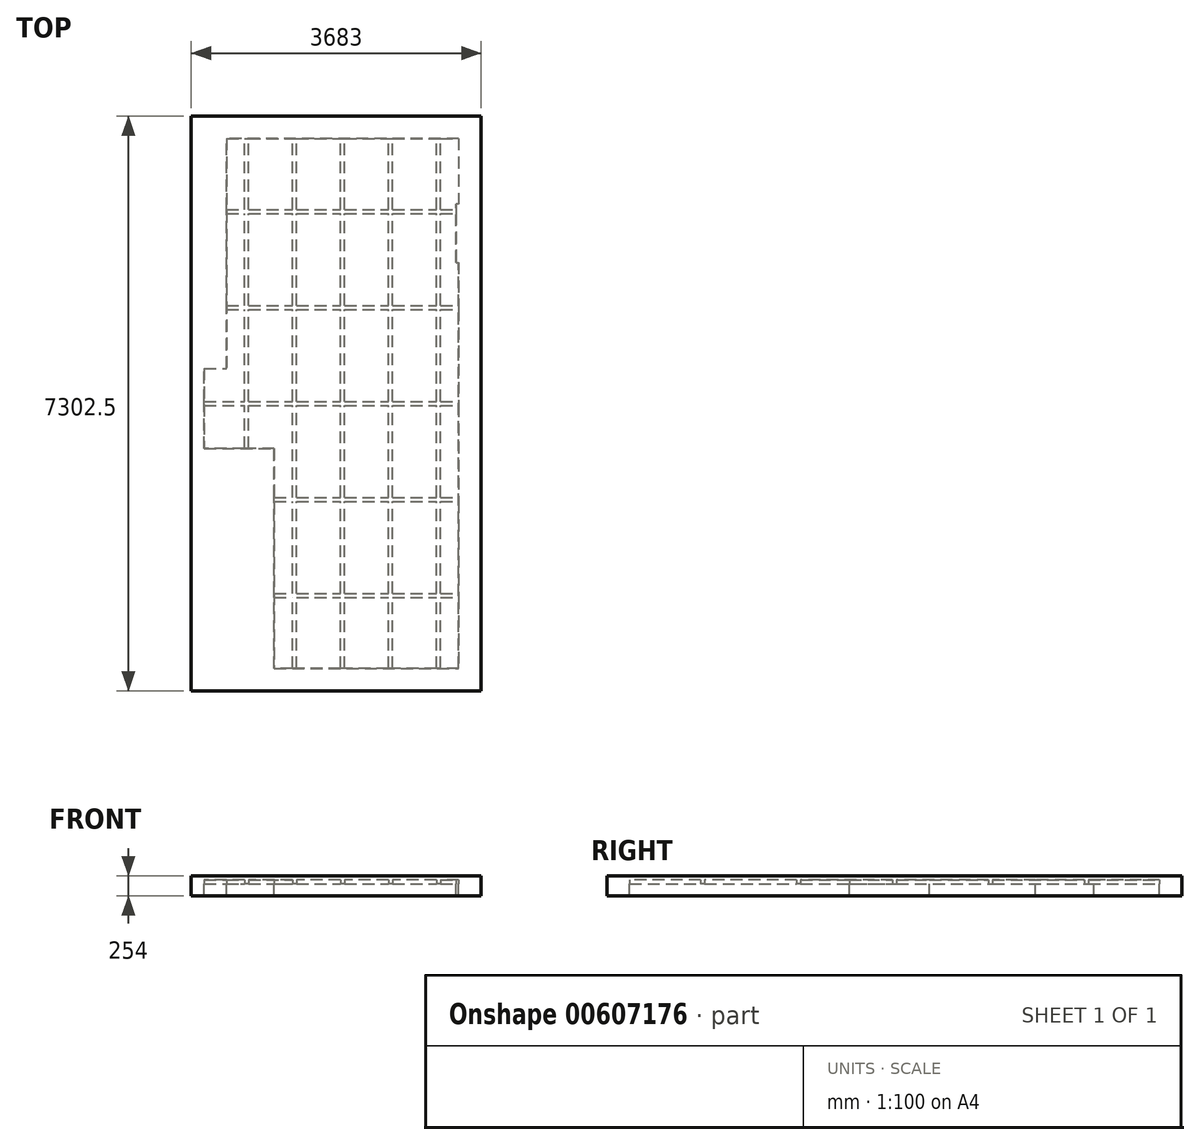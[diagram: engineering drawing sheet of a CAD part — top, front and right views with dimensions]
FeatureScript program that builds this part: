
annotation { "Feature Type Name" : "Feature", "Feature Type Description" : "" }
export const myFeature = defineFeature(function(context is Context, id is Id, definition is map)
    precondition{}
    {
        {
            var Q0;
            Q0=qCreatedBy(makeId("Top.planeOp"),FACE);
            var sketch = newSketch(context, id + "F0", { "sketchPlane" : qUnion([Q0])});
            skLineSegment(sketch, "E0", {"start": v(0, 0) * mm, "end": v(0, 5156.2) * mm});
            skLineSegment(sketch, "E1", {"start": v(0, 5156.2) * mm, "end": v(-34.92, 5156.2) * mm});
            skLineSegment(sketch, "E2", {"start": v(-34.92, 5156.2) * mm, "end": v(-34.92, 5899.15) * mm});
            skLineSegment(sketch, "E3", {"start": v(-34.92, 5899.15) * mm, "end": v(0, 5899.15) * mm});
            skLineSegment(sketch, "E4", {"start": v(0, 5899.15) * mm, "end": v(0, 6731) * mm});
            skLineSegment(sketch, "E5", {"start": v(0, 6731) * mm, "end": v(-2946.4, 6731) * mm});
            skLineSegment(sketch, "E6", {"start": v(-2946.4, 6731) * mm, "end": v(-2946.4, 3810) * mm});
            skLineSegment(sketch, "E7", {"start": v(-2946.4, 3810) * mm, "end": v(-3232.15, 3810) * mm});
            skLineSegment(sketch, "E8", {"start": v(-3232.15, 3810) * mm, "end": v(-3232.15, 2794) * mm});
            skLineSegment(sketch, "E9", {"start": v(-3232.15, 2794) * mm, "end": v(-2343.15, 2794) * mm});
            skLineSegment(sketch, "E10", {"start": v(-2343.15, 2794) * mm, "end": v(-2343.15, 0) * mm});
            skLineSegment(sketch, "E11", {"start": v(-2343.15, 0) * mm, "end": v(0, 0) * mm});
            skLineSegment(sketch, "E12", {"start": v(285.75, 7016.75) * mm, "end": v(285.75, -285.75) * mm});
            skLineSegment(sketch, "E13", {"start": v(285.75, -285.75) * mm, "end": v(-3397.25, -285.75) * mm});
            skLineSegment(sketch, "E14", {"start": v(285.75, 7016.75) * mm, "end": v(-3397.25, 7016.75) * mm});
            skLineSegment(sketch, "E15", {"start": v(-3397.25, 7016.75) * mm, "end": v(-3397.25, -285.75) * mm});
            skSolve(sketch);
        }
        {
            var Q0;
            Q0=makeQuery(id+"F0.imprint","IMPRINT",FACE,{"disambiguationData":[TD([[makeQuery(id+"F0.imprint","IMPRINT",EDGE,{"derivedFrom":sQuery(id+"F0.wireOp",EDGE,"E0")}),-1.0]])]});
            extrude(context, id + "F1", {"entities" : qUnion([Q0]), "oppositeDirection" : true, "depth" : 254 * mm, "offsetDistance" : 25.4 * mm});
        }
        {
            var Q0;
            Q0=qSketchRegion(id+"F0",true);
            var Q1;
            Q1=makeQuery(id+"F0.imprint","IMPRINT",FACE,{"disambiguationData":[TD([[makeQuery(id+"F0.imprint","IMPRINT",EDGE,{"derivedFrom":sQuery(id+"F0.wireOp",EDGE,"E0")}),1.0]])]});
            extrude(context, id + "F2", {"entities" : qUnion([Q0, Q1]), "operationType" : NewBodyOperationType.ADD, "oppositeDirection" : true, "depth" : 101.6 * mm, "offsetDistance" : 25.4 * mm});
        }
        {
            var Q0;
            Q0=makeQuery(id+"F2.opExtrude","CAP_FACE",FACE,{"disambiguationData":[OSD([sQuery(id+"F0.wireOp",EDGE,"E12"),sQuery(id+"F0.wireOp",EDGE,"E13"),sQuery(id+"F0.wireOp",EDGE,"E14"),sQuery(id+"F0.wireOp",EDGE,"E15")])],"isStart":false});
            var sketch = newSketch(context, id + "F3", { "sketchPlane" : qUnion([Q0])});
            skLineSegment(sketch, "E16.bottom", {"start": v(-2060.58, 0) * mm, "end": v(-2111.38, 0) * mm});
            skLineSegment(sketch, "E16.top", {"start": v(-2060.57, -6731) * mm, "end": v(-2111.37, -6731) * mm});
            skLineSegment(sketch, "E16.left", {"start": v(-2060.58, 0) * mm, "end": v(-2060.58, -901.7) * mm});
            skLineSegment(sketch, "E17.bottom", {"start": v(-1450.98, 0) * mm, "end": v(-1501.78, 0) * mm});
            skLineSegment(sketch, "E17.top", {"start": v(-1450.97, -6731) * mm, "end": v(-1501.77, -6731) * mm});
            skLineSegment(sketch, "E17.left", {"start": v(-1450.98, 0) * mm, "end": v(-1450.98, -901.7) * mm});
            skLineSegment(sketch, "E17.right", {"start": v(-1501.78, 0) * mm, "end": v(-1501.78, -901.7) * mm});
            skPoint(sketch, "E18.oppositeSnap0", {"position": v(-892.18, 0) * mm});
            skLineSegment(sketch, "E18.bottom", {"start": v(-841.38, 0) * mm, "end": v(-892.18, 0) * mm});
            skLineSegment(sketch, "E18.top", {"start": v(-841.37, -6731) * mm, "end": v(-892.17, -6731) * mm});
            skLineSegment(sketch, "E18.left", {"start": v(-841.38, 0) * mm, "end": v(-841.38, -901.7) * mm});
            skLineSegment(sketch, "E18.right", {"start": v(-892.18, 0) * mm, "end": v(-892.18, -901.7) * mm});
            skLineSegment(sketch, "E19.bottom", {"start": v(-282.58, 0) * mm, "end": v(-231.78, 0) * mm});
            skLineSegment(sketch, "E19.top", {"start": v(-282.57, -6731) * mm, "end": v(-231.77, -6731) * mm});
            skLineSegment(sketch, "E19.left", {"start": v(-282.58, 0) * mm, "end": v(-282.57, -901.7) * mm});
            skLineSegment(sketch, "E19.right", {"start": v(-231.78, 0) * mm, "end": v(-231.77, -901.7) * mm});
            skLineSegment(sketch, "E20.bottom", {"start": v(-2720.98, -2794) * mm, "end": v(-2670.18, -2794) * mm});
            skLineSegment(sketch, "E20.top", {"start": v(-2720.98, -6731) * mm, "end": v(-2670.18, -6731) * mm});
            skLineSegment(sketch, "E20.left", {"start": v(-2720.98, -2794) * mm, "end": v(-2720.98, -3340.1) * mm});
            skLineSegment(sketch, "E20.right", {"start": v(-2670.18, -5829.3) * mm, "end": v(-2670.18, -6731) * mm});
            skLineSegment(sketch, "E21.bottom", {"start": v(-231.77, -5829.3) * mm, "end": v(-34.92, -5829.3) * mm});
            skLineSegment(sketch, "E21.top", {"start": v(-2946.4, -5778.5) * mm, "end": v(-2720.98, -5778.5) * mm});
            skLineSegment(sketch, "E21.left", {"start": v(-2946.4, -5829.3) * mm, "end": v(-2946.4, -5778.5) * mm});
            skLineSegment(sketch, "E21.right", {"start": v(-34.92, -5829.3) * mm, "end": v(-34.92, -5778.5) * mm});
            skLineSegment(sketch, "E22.bottom", {"start": v(-231.77, -4559.3) * mm, "end": v(0, -4559.3) * mm});
            skLineSegment(sketch, "E22.top", {"start": v(-2946.4, -4610.1) * mm, "end": v(-2720.98, -4610.1) * mm});
            skLineSegment(sketch, "E22.left", {"start": v(-2946.4, -4559.3) * mm, "end": v(-2946.4, -4610.1) * mm});
            skLineSegment(sketch, "E22.right", {"start": v(0, -4559.3) * mm, "end": v(0, -4610.1) * mm});
            skLineSegment(sketch, "E23.bottom", {"start": v(-3232.15, -3340.1) * mm, "end": v(-2720.98, -3340.1) * mm});
            skLineSegment(sketch, "E23.top", {"start": v(-3232.15, -3390.9) * mm, "end": v(-2720.98, -3390.9) * mm});
            skLineSegment(sketch, "E23.left", {"start": v(-3232.15, -3340.1) * mm, "end": v(-3232.15, -3390.9) * mm});
            skLineSegment(sketch, "E23.right", {"start": v(0, -3340.1) * mm, "end": v(0, -3390.9) * mm});
            skLineSegment(sketch, "E24.bottom", {"start": v(-231.77, -2120.9) * mm, "end": v(0, -2120.9) * mm});
            skLineSegment(sketch, "E24.top", {"start": v(-2343.15, -2171.7) * mm, "end": v(-2111.38, -2171.7) * mm});
            skLineSegment(sketch, "E24.left", {"start": v(-2343.15, -2120.9) * mm, "end": v(-2343.15, -2171.7) * mm});
            skLineSegment(sketch, "E24.right", {"start": v(0, -2120.9) * mm, "end": v(0, -2171.7) * mm});
            skLineSegment(sketch, "E25.bottom", {"start": v(-231.77, -901.7) * mm, "end": v(0, -901.7) * mm});
            skLineSegment(sketch, "E25.top", {"start": v(-2343.15, -952.5) * mm, "end": v(-2111.38, -952.5) * mm});
            skLineSegment(sketch, "E25.left", {"start": v(-2343.15, -901.7) * mm, "end": v(-2343.15, -952.5) * mm});
            skLineSegment(sketch, "E25.right", {"start": v(0, -901.7) * mm, "end": v(0, -952.5) * mm});
            skLineSegment(sketch, "E26.trimOffspring", {"start": v(-2111.38, 0) * mm, "end": v(-2111.38, -901.7) * mm});
            skLineSegment(sketch, "E27.trimOffspring", {"start": v(-2111.38, -952.5) * mm, "end": v(-2111.38, -2120.9) * mm});
            skLineSegment(sketch, "E28.trimOffspring", {"start": v(-2343.15, -901.7) * mm, "end": v(-2111.38, -901.7) * mm});
            skLineSegment(sketch, "E29.trimOffspring", {"start": v(-2060.58, -952.5) * mm, "end": v(-2060.57, -2120.9) * mm});
            skLineSegment(sketch, "E30.trimOffspring", {"start": v(-2060.58, -952.5) * mm, "end": v(-1501.78, -952.5) * mm});
            skLineSegment(sketch, "E31.trimOffspring", {"start": v(-1501.78, -952.5) * mm, "end": v(-1501.78, -2120.9) * mm});
            skLineSegment(sketch, "E32.trimOffspring", {"start": v(-2060.58, -901.7) * mm, "end": v(-1501.78, -901.7) * mm});
            skLineSegment(sketch, "E33.trimOffspring", {"start": v(-1450.98, -952.5) * mm, "end": v(-1450.98, -2120.9) * mm});
            skLineSegment(sketch, "E34.trimOffspring", {"start": v(-1450.98, -952.5) * mm, "end": v(-892.18, -952.5) * mm});
            skLineSegment(sketch, "E35.trimOffspring", {"start": v(-1450.98, -901.7) * mm, "end": v(-892.18, -901.7) * mm});
            skLineSegment(sketch, "E36.trimOffspring", {"start": v(-892.18, -952.5) * mm, "end": v(-892.18, -2120.9) * mm});
            skLineSegment(sketch, "E37.trimOffspring", {"start": v(-841.38, -952.5) * mm, "end": v(-282.58, -952.5) * mm});
            skLineSegment(sketch, "E38.trimOffspring", {"start": v(-841.38, -952.5) * mm, "end": v(-841.38, -2120.9) * mm});
            skLineSegment(sketch, "E39.trimOffspring", {"start": v(-841.38, -901.7) * mm, "end": v(-282.58, -901.7) * mm});
            skLineSegment(sketch, "E40.trimOffspring", {"start": v(-282.57, -952.5) * mm, "end": v(-282.57, -2120.9) * mm});
            skLineSegment(sketch, "E41.trimOffspring", {"start": v(-231.77, -952.5) * mm, "end": v(0, -952.5) * mm});
            skLineSegment(sketch, "E42.trimOffspring", {"start": v(-231.77, -952.5) * mm, "end": v(-231.77, -2120.9) * mm});
            skLineSegment(sketch, "E43.trimOffspring", {"start": v(-2111.38, -2171.7) * mm, "end": v(-2111.38, -3340.1) * mm});
            skLineSegment(sketch, "E44.trimOffspring", {"start": v(-2343.15, -2120.9) * mm, "end": v(-2111.38, -2120.9) * mm});
            skLineSegment(sketch, "E45.trimOffspring", {"start": v(-2060.57, -2171.7) * mm, "end": v(-2060.57, -3340.1) * mm});
            skLineSegment(sketch, "E46.trimOffspring", {"start": v(-2060.57, -2171.7) * mm, "end": v(-1501.78, -2171.7) * mm});
            skLineSegment(sketch, "E47.trimOffspring", {"start": v(-1501.78, -2171.7) * mm, "end": v(-1501.77, -3340.1) * mm});
            skLineSegment(sketch, "E48.trimOffspring", {"start": v(-2060.57, -2120.9) * mm, "end": v(-1501.78, -2120.9) * mm});
            skLineSegment(sketch, "E49.trimOffspring", {"start": v(-1450.98, -2171.7) * mm, "end": v(-1450.97, -3340.1) * mm});
            skLineSegment(sketch, "E50.trimOffspring", {"start": v(-1450.98, -2171.7) * mm, "end": v(-892.18, -2171.7) * mm});
            skLineSegment(sketch, "E51.trimOffspring", {"start": v(-892.18, -2171.7) * mm, "end": v(-892.18, -3340.1) * mm});
            skLineSegment(sketch, "E52.trimOffspring", {"start": v(-1450.98, -2120.9) * mm, "end": v(-892.18, -2120.9) * mm});
            skLineSegment(sketch, "E53.trimOffspring", {"start": v(-841.38, -2171.7) * mm, "end": v(-841.37, -3340.1) * mm});
            skLineSegment(sketch, "E54.trimOffspring", {"start": v(-841.38, -2171.7) * mm, "end": v(-282.57, -2171.7) * mm});
            skLineSegment(sketch, "E55.trimOffspring", {"start": v(-282.57, -2171.7) * mm, "end": v(-282.57, -3340.1) * mm});
            skLineSegment(sketch, "E56.trimOffspring", {"start": v(-841.38, -2120.9) * mm, "end": v(-282.57, -2120.9) * mm});
            skLineSegment(sketch, "E57.trimOffspring", {"start": v(-231.77, -2171.7) * mm, "end": v(-231.77, -3340.1) * mm});
            skLineSegment(sketch, "E58.trimOffspring", {"start": v(-231.77, -2171.7) * mm, "end": v(0, -2171.7) * mm});
            skLineSegment(sketch, "E59.trimOffspring", {"start": v(-2720.98, -3390.9) * mm, "end": v(-2720.98, -4559.3) * mm});
            skLineSegment(sketch, "E60.trimOffspring", {"start": v(-2670.18, -3340.1) * mm, "end": v(-2111.38, -3340.1) * mm});
            skLineSegment(sketch, "E61.trimOffspring", {"start": v(-2670.18, -2794) * mm, "end": v(-2670.18, -3340.1) * mm});
            skLineSegment(sketch, "E62.trimOffspring", {"start": v(-2670.18, -3390.9) * mm, "end": v(-2111.38, -3390.9) * mm});
            skLineSegment(sketch, "E63.trimOffspring", {"start": v(-2111.38, -3390.9) * mm, "end": v(-2111.37, -4559.3) * mm});
            skLineSegment(sketch, "E64.trimOffspring", {"start": v(-2060.57, -3340.1) * mm, "end": v(-1501.77, -3340.1) * mm});
            skLineSegment(sketch, "E65.trimOffspring", {"start": v(-2060.57, -3390.9) * mm, "end": v(-2060.57, -4559.3) * mm});
            skLineSegment(sketch, "E66.trimOffspring", {"start": v(-2060.57, -3390.9) * mm, "end": v(-1501.77, -3390.9) * mm});
            skLineSegment(sketch, "E67.trimOffspring", {"start": v(-1501.77, -3390.9) * mm, "end": v(-1501.77, -4559.3) * mm});
            skLineSegment(sketch, "E68.trimOffspring", {"start": v(-1450.97, -3340.1) * mm, "end": v(-892.18, -3340.1) * mm});
            skLineSegment(sketch, "E69.trimOffspring", {"start": v(-1450.97, -3390.9) * mm, "end": v(-1450.97, -4559.3) * mm});
            skLineSegment(sketch, "E70.trimOffspring", {"start": v(-1450.97, -3390.9) * mm, "end": v(-892.18, -3390.9) * mm});
            skLineSegment(sketch, "E71.trimOffspring", {"start": v(-892.18, -3390.9) * mm, "end": v(-892.17, -4559.3) * mm});
            skLineSegment(sketch, "E72.trimOffspring", {"start": v(-841.37, -3340.1) * mm, "end": v(-282.57, -3340.1) * mm});
            skLineSegment(sketch, "E73.trimOffspring", {"start": v(-841.37, -3390.9) * mm, "end": v(-841.37, -4559.3) * mm});
            skLineSegment(sketch, "E74.trimOffspring", {"start": v(-841.37, -3390.9) * mm, "end": v(-282.57, -3390.9) * mm});
            skLineSegment(sketch, "E75.trimOffspring", {"start": v(-282.57, -3390.9) * mm, "end": v(-282.57, -4559.3) * mm});
            skLineSegment(sketch, "E76.trimOffspring", {"start": v(-231.77, -3340.1) * mm, "end": v(0, -3340.1) * mm});
            skLineSegment(sketch, "E77.trimOffspring", {"start": v(-231.77, -3390.9) * mm, "end": v(-231.77, -4559.3) * mm});
            skLineSegment(sketch, "E78.trimOffspring", {"start": v(-231.77, -3390.9) * mm, "end": v(0, -3390.9) * mm});
            skLineSegment(sketch, "E79.trimOffspring", {"start": v(-2720.98, -4610.1) * mm, "end": v(-2720.98, -5778.5) * mm});
            skLineSegment(sketch, "E80.trimOffspring", {"start": v(-2946.4, -4559.3) * mm, "end": v(-2720.98, -4559.3) * mm});
            skLineSegment(sketch, "E81.trimOffspring", {"start": v(-2670.18, -3390.9) * mm, "end": v(-2670.18, -4559.3) * mm});
            skLineSegment(sketch, "E82.trimOffspring", {"start": v(-2670.18, -4610.1) * mm, "end": v(-2111.37, -4610.1) * mm});
            skLineSegment(sketch, "E83.trimOffspring", {"start": v(-2111.37, -4610.1) * mm, "end": v(-2111.37, -5778.5) * mm});
            skLineSegment(sketch, "E84.trimOffspring", {"start": v(-2670.18, -4559.3) * mm, "end": v(-2111.37, -4559.3) * mm});
            skLineSegment(sketch, "E85.trimOffspring", {"start": v(-2060.57, -4610.1) * mm, "end": v(-2060.57, -5778.5) * mm});
            skLineSegment(sketch, "E86.trimOffspring", {"start": v(-2060.57, -4610.1) * mm, "end": v(-1501.77, -4610.1) * mm});
            skLineSegment(sketch, "E87.trimOffspring", {"start": v(-1501.77, -4610.1) * mm, "end": v(-1501.77, -5778.5) * mm});
            skLineSegment(sketch, "E88.trimOffspring", {"start": v(-2060.57, -4559.3) * mm, "end": v(-1501.77, -4559.3) * mm});
            skLineSegment(sketch, "E89.trimOffspring", {"start": v(-1450.97, -4610.1) * mm, "end": v(-1450.97, -5778.5) * mm});
            skLineSegment(sketch, "E90.trimOffspring", {"start": v(-1450.97, -4610.1) * mm, "end": v(-892.17, -4610.1) * mm});
            skLineSegment(sketch, "E91.trimOffspring", {"start": v(-892.17, -4610.1) * mm, "end": v(-892.17, -5778.5) * mm});
            skLineSegment(sketch, "E92.trimOffspring", {"start": v(-1450.97, -4559.3) * mm, "end": v(-892.17, -4559.3) * mm});
            skLineSegment(sketch, "E93.trimOffspring", {"start": v(-841.37, -4610.1) * mm, "end": v(-841.37, -5778.5) * mm});
            skLineSegment(sketch, "E94.trimOffspring", {"start": v(-841.37, -4610.1) * mm, "end": v(-282.57, -4610.1) * mm});
            skLineSegment(sketch, "E95.trimOffspring", {"start": v(-282.57, -4610.1) * mm, "end": v(-282.57, -5778.5) * mm});
            skLineSegment(sketch, "E96.trimOffspring", {"start": v(-841.37, -4559.3) * mm, "end": v(-282.57, -4559.3) * mm});
            skLineSegment(sketch, "E97.trimOffspring", {"start": v(-231.77, -4610.1) * mm, "end": v(-231.77, -5778.5) * mm});
            skLineSegment(sketch, "E98.trimOffspring", {"start": v(-231.77, -4610.1) * mm, "end": v(0, -4610.1) * mm});
            skLineSegment(sketch, "E99.trimOffspring", {"start": v(-2720.98, -5829.3) * mm, "end": v(-2720.98, -6731) * mm});
            skLineSegment(sketch, "E100.trimOffspring", {"start": v(-2670.18, -5778.5) * mm, "end": v(-2111.37, -5778.5) * mm});
            skLineSegment(sketch, "E101.trimOffspring", {"start": v(-2670.18, -4610.1) * mm, "end": v(-2670.18, -5778.5) * mm});
            skLineSegment(sketch, "E102.trimOffspring", {"start": v(-2946.4, -5829.3) * mm, "end": v(-2720.98, -5829.3) * mm});
            skLineSegment(sketch, "E103.trimOffspring", {"start": v(-2111.37, -5829.3) * mm, "end": v(-2111.37, -6731) * mm});
            skLineSegment(sketch, "E104.trimOffspring", {"start": v(-2060.57, -5778.5) * mm, "end": v(-1501.77, -5778.5) * mm});
            skLineSegment(sketch, "E105.trimOffspring", {"start": v(-2060.57, -5829.3) * mm, "end": v(-2060.57, -6731) * mm});
            skLineSegment(sketch, "E106.trimOffspring", {"start": v(-2670.18, -5829.3) * mm, "end": v(-2111.37, -5829.3) * mm});
            skLineSegment(sketch, "E107.trimOffspring", {"start": v(-1501.77, -5829.3) * mm, "end": v(-1501.77, -6731) * mm});
            skLineSegment(sketch, "E108.trimOffspring", {"start": v(-1450.97, -5778.5) * mm, "end": v(-892.17, -5778.5) * mm});
            skLineSegment(sketch, "E109.trimOffspring", {"start": v(-1450.97, -5829.3) * mm, "end": v(-1450.97, -6731) * mm});
            skLineSegment(sketch, "E110.trimOffspring", {"start": v(-2060.57, -5829.3) * mm, "end": v(-1501.77, -5829.3) * mm});
            skLineSegment(sketch, "E111.trimOffspring", {"start": v(-892.17, -5829.3) * mm, "end": v(-892.17, -6731) * mm});
            skLineSegment(sketch, "E112.trimOffspring", {"start": v(-841.37, -5778.5) * mm, "end": v(-282.57, -5778.5) * mm});
            skLineSegment(sketch, "E113.trimOffspring", {"start": v(-841.37, -5829.3) * mm, "end": v(-841.37, -6731) * mm});
            skLineSegment(sketch, "E114.trimOffspring", {"start": v(-1450.97, -5829.3) * mm, "end": v(-892.17, -5829.3) * mm});
            skLineSegment(sketch, "E115.trimOffspring", {"start": v(-282.57, -5829.3) * mm, "end": v(-282.57, -6731) * mm});
            skLineSegment(sketch, "E116.trimOffspring", {"start": v(-231.77, -5778.5) * mm, "end": v(-34.92, -5778.5) * mm});
            skLineSegment(sketch, "E117.trimOffspring", {"start": v(-231.77, -5829.3) * mm, "end": v(-231.77, -6731) * mm});
            skLineSegment(sketch, "E118.trimOffspring", {"start": v(-841.37, -5829.3) * mm, "end": v(-282.57, -5829.3) * mm});
            skSolve(sketch);
        }
        {
            var Q0;
            {var subQ0=sQuery(id+"F3.wireOp",EDGE,"E16.right");Q0=makeQuery(id+"F3.imprint","IMPRINT",FACE,{"disambiguationData":[TD([[makeQuery(id+"F3.imprint","IMPRINT",EDGE,{"derivedFrom":subQ0}),-1.0]])]});}
            var Q1;
            {var subQ0=sQuery(id+"F3.wireOp",EDGE,"E16.left");Q1=makeQuery(id+"F3.imprint","IMPRINT",FACE,{"disambiguationData":[TD([[makeQuery(id+"F3.imprint","IMPRINT",EDGE,{"derivedFrom":subQ0}),1.0]])]});}
            var Q2;
            {var subQ0=sQuery(id+"F3.wireOp",EDGE,"E17.left");Q2=makeQuery(id+"F3.imprint","IMPRINT",FACE,{"disambiguationData":[TD([[makeQuery(id+"F3.imprint","IMPRINT",EDGE,{"derivedFrom":subQ0}),1.0]])]});}
            var Q3;
            {var subQ0=sQuery(id+"F3.wireOp",EDGE,"E18.left");Q3=makeQuery(id+"F3.imprint","IMPRINT",FACE,{"disambiguationData":[TD([[makeQuery(id+"F3.imprint","IMPRINT",EDGE,{"derivedFrom":subQ0}),1.0]])]});}
            var Q4;
            {var subQ0=sQuery(id+"F3.wireOp",EDGE,"E19.right");Q4=makeQuery(id+"F3.imprint","IMPRINT",FACE,{"disambiguationData":[TD([[makeQuery(id+"F3.imprint","IMPRINT",EDGE,{"derivedFrom":subQ0}),1.0]])]});}
            var Q5;
            Q5=makeQuery(id+"F3.imprint","IMPRINT",FACE,{"disambiguationData":[TD([[makeQuery(id+"F3.imprint","IMPRINT",EDGE,{"derivedFrom":sQuery(id+"F3.wireOp",EDGE,"5275577d-fd46-436c-945e-631875000ced.trimOffspring")}),1.0]])]});
            var Q6;
            Q6=makeQuery(id+"F3.imprint","IMPRINT",FACE,{"disambiguationData":[TD([[makeQuery(id+"F3.imprint","IMPRINT",EDGE,{"derivedFrom":sQuery(id+"F3.wireOp",EDGE,"5d5d9ea1-b980-4400-a40e-6dee1850f65f.trimOffspring")}),-1.0]])]});
            var Q7;
            Q7=makeQuery(id+"F3.imprint","IMPRINT",FACE,{"disambiguationData":[TD([[makeQuery(id+"F3.imprint","IMPRINT",EDGE,{"derivedFrom":sQuery(id+"F3.wireOp",EDGE,"419a1927-79ba-4876-a8ca-a9a6843eeb37.trimOffspring")}),1.0]])]});
            var Q8;
            Q8=makeQuery(id+"F3.imprint","IMPRINT",FACE,{"disambiguationData":[TD([[makeQuery(id+"F3.imprint","IMPRINT",EDGE,{"derivedFrom":sQuery(id+"F3.wireOp",EDGE,"7147acea-72a4-4ae8-9284-f976fcfd3f97.trimOffspring")}),1.0]])]});
            var Q9;
            {var subQ0=sQuery(id+"F3.wireOp",EDGE,"E25.bottom");Q9=makeQuery(id+"F3.imprint","IMPRINT",FACE,{"disambiguationData":[TD([[makeQuery(id+"F3.imprint","IMPRINT",EDGE,{"derivedFrom":subQ0}),1.0]])]});}
            var Q10;
            {var subQ0=sQuery(id+"F3.wireOp",EDGE,"jnkveo8h-34Qn-uZse-wEQl-v94LyAbfYETq.bottom");Q10=makeQuery(id+"F3.imprint","IMPRINT",FACE,{"disambiguationData":[TD([[makeQuery(id+"F3.imprint","IMPRINT",EDGE,{"derivedFrom":subQ0}),1.0]])]});}
            var Q11;
            Q11=makeQuery(id+"F3.imprint","IMPRINT",FACE,{"disambiguationData":[TD([[makeQuery(id+"F3.imprint","IMPRINT",EDGE,{"derivedFrom":sQuery(id+"F3.wireOp",EDGE,"97d052bb-f3c9-43e7-bdd4-73ddd512fd27.trimOffspring")}),-1.0]])]});
            var Q12;
            Q12=makeQuery(id+"F3.imprint","IMPRINT",FACE,{"disambiguationData":[TD([[makeQuery(id+"F3.imprint","IMPRINT",EDGE,{"derivedFrom":sQuery(id+"F3.wireOp",EDGE,"7579f699-3f1e-4c33-9fa8-31185bab74d0.trimOffspring")}),-1.0]])]});
            var Q13;
            Q13=makeQuery(id+"F3.imprint","IMPRINT",FACE,{"disambiguationData":[TD([[makeQuery(id+"F3.imprint","IMPRINT",EDGE,{"derivedFrom":sQuery(id+"F3.wireOp",EDGE,"6304ff67-14fa-4887-9a69-17be51c6297e.trimOffspring")}),-1.0]])]});
            var Q14;
            {var subQ0=sQuery(id+"F3.wireOp",EDGE,"d1431141-8a29-4ed9-86f8-9a50813f61a8.trimOffspring");Q14=makeQuery(id+"F3.imprint","IMPRINT",FACE,{"disambiguationData":[TD([[makeQuery(id+"F3.imprint","IMPRINT",EDGE,{"derivedFrom":subQ0}),-1.0]])]});}
            var Q15;
            Q15=makeQuery(id+"F3.imprint","IMPRINT",FACE,{"disambiguationData":[TD([[makeQuery(id+"F3.imprint","IMPRINT",EDGE,{"derivedFrom":sQuery(id+"F3.wireOp",EDGE,"a5f1d1d1-a92c-4c51-81e6-e19ced365f34.trimOffspring")}),1.0]])]});
            var Q16;
            Q16=makeQuery(id+"F3.imprint","IMPRINT",FACE,{"disambiguationData":[TD([[makeQuery(id+"F3.imprint","IMPRINT",EDGE,{"derivedFrom":sQuery(id+"F3.wireOp",EDGE,"71ca613b-0385-4ede-9753-ab078624ce6d.trimOffspring")}),1.0]])]});
            var Q17;
            Q17=makeQuery(id+"F3.imprint","IMPRINT",FACE,{"disambiguationData":[TD([[makeQuery(id+"F3.imprint","IMPRINT",EDGE,{"derivedFrom":sQuery(id+"F3.wireOp",EDGE,"89b79296-b87a-42a5-92d1-10b9b3886754.trimOffspring")}),1.0]])]});
            var Q18;
            Q18=makeQuery(id+"F3.imprint","IMPRINT",FACE,{"disambiguationData":[TD([[makeQuery(id+"F3.imprint","IMPRINT",EDGE,{"derivedFrom":sQuery(id+"F3.wireOp",EDGE,"2bdae874-39bd-468b-bbb6-3c811ffc38b8.trimOffspring")}),1.0]])]});
            var Q19;
            {var subQ0=sQuery(id+"F3.wireOp",EDGE,"E24.bottom");Q19=makeQuery(id+"F3.imprint","IMPRINT",FACE,{"disambiguationData":[TD([[makeQuery(id+"F3.imprint","IMPRINT",EDGE,{"derivedFrom":subQ0}),1.0]])]});}
            var Q20;
            {var subQ4=sQuery(id+"F3.wireOp",EDGE,"E24.top");Q20=makeQuery(id+"F3.imprint","IMPRINT",FACE,{"disambiguationData":[TD([[makeQuery(id+"F3.imprint","IMPRINT",EDGE,{"derivedFrom":subQ4}),-1.0]])]});}
            var Q21;
            Q21=makeQuery(id+"F3.imprint","IMPRINT",FACE,{"disambiguationData":[TD([[makeQuery(id+"F3.imprint","IMPRINT",EDGE,{"derivedFrom":sQuery(id+"F3.wireOp",EDGE,"39c06717-3cbb-4c5a-a606-887fb9b17794.trimOffspring")}),1.0]])]});
            var Q22;
            {var subQ0=sQuery(id+"F3.wireOp",EDGE,"73e70683-5ee5-46d8-866f-819bddcc5298.trimOffspring");Q22=makeQuery(id+"F3.imprint","IMPRINT",FACE,{"disambiguationData":[TD([[makeQuery(id+"F3.imprint","IMPRINT",EDGE,{"derivedFrom":subQ0}),1.0]])]});}
            var Q23;
            {var subQ5=sQuery(id+"F3.wireOp",EDGE,"c712e656-0eac-4d00-bb53-271c885fea4c.trimOffspring");Q23=makeQuery(id+"F3.imprint","IMPRINT",FACE,{"disambiguationData":[TD([[makeQuery(id+"F3.imprint","IMPRINT",EDGE,{"derivedFrom":subQ5}),-1.0]])]});}
            var Q24;
            {var subQ5=sQuery(id+"F3.wireOp",EDGE,"33cf923b-17e3-46e0-9c64-5ad1de0c345c.trimOffspring");Q24=makeQuery(id+"F3.imprint","IMPRINT",FACE,{"disambiguationData":[TD([[makeQuery(id+"F3.imprint","IMPRINT",EDGE,{"derivedFrom":subQ5}),-1.0]])]});}
            var Q25;
            {var subQ5=sQuery(id+"F3.wireOp",EDGE,"bb10438d-eeba-44aa-a871-abd86f6ddf24.trimOffspring");Q25=makeQuery(id+"F3.imprint","IMPRINT",FACE,{"disambiguationData":[TD([[makeQuery(id+"F3.imprint","IMPRINT",EDGE,{"derivedFrom":subQ5}),1.0]])]});}
            var Q26;
            {var subQ5=sQuery(id+"F3.wireOp",EDGE,"52d7eeea-90b6-4823-aa46-ec4d873f9261.trimOffspring");Q26=makeQuery(id+"F3.imprint","IMPRINT",FACE,{"disambiguationData":[TD([[makeQuery(id+"F3.imprint","IMPRINT",EDGE,{"derivedFrom":subQ5}),1.0]])]});}
            var Q27;
            {var subQ0=sQuery(id+"F3.wireOp",EDGE,"4be3ee05-e835-430b-86e3-95df6af259d1.trimOffspring");Q27=makeQuery(id+"F3.imprint","IMPRINT",FACE,{"disambiguationData":[TD([[makeQuery(id+"F3.imprint","IMPRINT",EDGE,{"derivedFrom":subQ0}),1.0]])]});}
            var Q28;
            {var subQ0=sQuery(id+"F3.wireOp",EDGE,"94a81156-8c84-4297-9fe8-a2b989827e89.trimOffspring");Q28=makeQuery(id+"F3.imprint","IMPRINT",FACE,{"disambiguationData":[TD([[makeQuery(id+"F3.imprint","IMPRINT",EDGE,{"derivedFrom":subQ0}),1.0]])]});}
            var Q29;
            {var subQ4=sQuery(id+"F3.wireOp",EDGE,"62d13280-0fc4-48c6-a3ad-ad07ee72a325.trimOffspring");Q29=makeQuery(id+"F3.imprint","IMPRINT",FACE,{"disambiguationData":[TD([[makeQuery(id+"F3.imprint","IMPRINT",EDGE,{"derivedFrom":subQ4}),-1.0]])]});}
            var Q30;
            {var subQ0=sQuery(id+"F3.wireOp",EDGE,"E23.bottom");Q30=makeQuery(id+"F3.imprint","IMPRINT",FACE,{"disambiguationData":[TD([[makeQuery(id+"F3.imprint","IMPRINT",EDGE,{"derivedFrom":subQ0}),1.0]])]});}
            var Q31;
            {var subQ2=sQuery(id+"F3.wireOp",EDGE,"vw6nCLHd-BdX1-Cp7E-QXN7-itVFLqW1L8Wl.bottom");Q31=makeQuery(id+"F3.imprint","IMPRINT",FACE,{"disambiguationData":[TD([[makeQuery(id+"F3.imprint","IMPRINT",EDGE,{"derivedFrom":subQ2}),1.0]])]});}
            var Q32;
            Q32=makeQuery(id+"F3.imprint","IMPRINT",FACE,{"disambiguationData":[TD([[makeQuery(id+"F3.imprint","IMPRINT",EDGE,{"derivedFrom":sQuery(id+"F3.wireOp",EDGE,"176304b1-c81a-4d09-8947-c0923f52610c.trimOffspring")}),1.0]])]});
            var Q33;
            Q33=makeQuery(id+"F3.imprint","IMPRINT",FACE,{"disambiguationData":[TD([[makeQuery(id+"F3.imprint","IMPRINT",EDGE,{"derivedFrom":sQuery(id+"F3.wireOp",EDGE,"8417e929-2d85-4ff7-a4d6-1ddfbbc49de2.trimOffspring")}),1.0]])]});
            var Q34;
            Q34=makeQuery(id+"F3.imprint","IMPRINT",FACE,{"disambiguationData":[TD([[makeQuery(id+"F3.imprint","IMPRINT",EDGE,{"derivedFrom":sQuery(id+"F3.wireOp",EDGE,"4fb1bebd-5a60-40a3-9b48-382586a06392.trimOffspring")}),1.0]])]});
            var Q35;
            Q35=makeQuery(id+"F3.imprint","IMPRINT",FACE,{"disambiguationData":[TD([[makeQuery(id+"F3.imprint","IMPRINT",EDGE,{"derivedFrom":sQuery(id+"F3.wireOp",EDGE,"36db2874-cf93-4798-998c-2668608916af.trimOffspring")}),-1.0]])]});
            var Q36;
            Q36=makeQuery(id+"F3.imprint","IMPRINT",FACE,{"disambiguationData":[TD([[makeQuery(id+"F3.imprint","IMPRINT",EDGE,{"derivedFrom":sQuery(id+"F3.wireOp",EDGE,"6d28a154-f991-4222-b086-bb5232d831af.trimOffspring")}),1.0]])]});
            var Q37;
            {var subQ0=sQuery(id+"F3.wireOp",EDGE,"E22.bottom");Q37=makeQuery(id+"F3.imprint","IMPRINT",FACE,{"disambiguationData":[TD([[makeQuery(id+"F3.imprint","IMPRINT",EDGE,{"derivedFrom":subQ0}),1.0]])]});}
            var Q38;
            Q38=makeQuery(id+"F3.imprint","IMPRINT",FACE,{"disambiguationData":[TD([[makeQuery(id+"F3.imprint","IMPRINT",EDGE,{"derivedFrom":sQuery(id+"F3.wireOp",EDGE,"7d2c070a-92f7-4495-9d7a-3350c856e8d5.trimOffspring")}),-1.0]])]});
            var Q39;
            Q39=makeQuery(id+"F3.imprint","IMPRINT",FACE,{"disambiguationData":[TD([[makeQuery(id+"F3.imprint","IMPRINT",EDGE,{"derivedFrom":sQuery(id+"F3.wireOp",EDGE,"49242e2e-03a4-4838-a89b-9321c4de9e2a.trimOffspring")}),-1.0]])]});
            var Q40;
            Q40=makeQuery(id+"F3.imprint","IMPRINT",FACE,{"disambiguationData":[TD([[makeQuery(id+"F3.imprint","IMPRINT",EDGE,{"derivedFrom":sQuery(id+"F3.wireOp",EDGE,"bb379298-1c9c-4d33-a424-a5ad9235aa2c.trimOffspring")}),-1.0]])]});
            var Q41;
            Q41=makeQuery(id+"F3.imprint","IMPRINT",FACE,{"disambiguationData":[TD([[makeQuery(id+"F3.imprint","IMPRINT",EDGE,{"derivedFrom":sQuery(id+"F3.wireOp",EDGE,"26fff39a-1d8e-46b4-98f5-4e9366a7eae9.trimOffspring")}),-1.0]])]});
            var Q42;
            Q42=makeQuery(id+"F3.imprint","IMPRINT",FACE,{"disambiguationData":[TD([[makeQuery(id+"F3.imprint","IMPRINT",EDGE,{"derivedFrom":sQuery(id+"F3.wireOp",EDGE,"602905c4-ca09-4ee7-b83e-e295a0184bf6.trimOffspring")}),1.0]])]});
            var Q43;
            Q43=makeQuery(id+"F3.imprint","IMPRINT",FACE,{"disambiguationData":[TD([[makeQuery(id+"F3.imprint","IMPRINT",EDGE,{"derivedFrom":sQuery(id+"F3.wireOp",EDGE,"e275f461-bfcf-4590-8212-f15e47489e1a.trimOffspring")}),1.0]])]});
            var Q44;
            Q44=makeQuery(id+"F3.imprint","IMPRINT",FACE,{"disambiguationData":[TD([[makeQuery(id+"F3.imprint","IMPRINT",EDGE,{"derivedFrom":sQuery(id+"F3.wireOp",EDGE,"d10f1888-8964-4f65-921e-b60fecd54131.trimOffspring")}),-1.0]])]});
            var Q45;
            Q45=makeQuery(id+"F3.imprint","IMPRINT",FACE,{"disambiguationData":[TD([[makeQuery(id+"F3.imprint","IMPRINT",EDGE,{"derivedFrom":sQuery(id+"F3.wireOp",EDGE,"5be38015-2946-478a-a598-d27d1e9593ad.trimOffspring")}),1.0]])]});
            var Q46;
            Q46=makeQuery(id+"F3.imprint","IMPRINT",FACE,{"disambiguationData":[TD([[makeQuery(id+"F3.imprint","IMPRINT",EDGE,{"derivedFrom":sQuery(id+"F3.wireOp",EDGE,"7210623e-2327-4e53-ba5a-ab675f2d6065.trimOffspring")}),1.0]])]});
            var Q47;
            Q47=makeQuery(id+"F3.imprint","IMPRINT",FACE,{"disambiguationData":[TD([[makeQuery(id+"F3.imprint","IMPRINT",EDGE,{"derivedFrom":sQuery(id+"F3.wireOp",EDGE,"d6902397-3210-4650-a53e-7f9fc8e01979.trimOffspring")}),1.0]])]});
            var Q48;
            {var subQ0=sQuery(id+"F3.wireOp",EDGE,"VIWDZmOY-xdJ7-eMOP-5TMz-k7TIXh4QuG7M.top");Q48=makeQuery(id+"F3.imprint","IMPRINT",FACE,{"disambiguationData":[TD([[makeQuery(id+"F3.imprint","IMPRINT",EDGE,{"derivedFrom":subQ0}),1.0]])]});}
            var Q49;
            {var subQ0=sQuery(id+"F3.wireOp",EDGE,"E21.top");Q49=makeQuery(id+"F3.imprint","IMPRINT",FACE,{"disambiguationData":[TD([[makeQuery(id+"F3.imprint","IMPRINT",EDGE,{"derivedFrom":subQ0}),1.0]])]});}
            var Q50;
            Q50=makeQuery(id+"F3.imprint","IMPRINT",FACE,{"disambiguationData":[TD([[makeQuery(id+"F3.imprint","IMPRINT",EDGE,{"derivedFrom":sQuery(id+"F3.wireOp",EDGE,"8a304a7a-fab9-4c7e-86bd-6ae23d76b27a.trimOffspring")}),-1.0]])]});
            var Q51;
            Q51=makeQuery(id+"F3.imprint","IMPRINT",FACE,{"disambiguationData":[TD([[makeQuery(id+"F3.imprint","IMPRINT",EDGE,{"derivedFrom":sQuery(id+"F3.wireOp",EDGE,"910fd681-1d49-431d-8658-44434bddb2c7.trimOffspring")}),1.0]])]});
            var Q52;
            Q52=makeQuery(id+"F3.imprint","IMPRINT",FACE,{"disambiguationData":[TD([[makeQuery(id+"F3.imprint","IMPRINT",EDGE,{"derivedFrom":sQuery(id+"F3.wireOp",EDGE,"910d4fc7-1cc6-4588-9358-45c4361fa9ce.trimOffspring")}),1.0]])]});
            var Q53;
            Q53=makeQuery(id+"F3.imprint","IMPRINT",FACE,{"disambiguationData":[TD([[makeQuery(id+"F3.imprint","IMPRINT",EDGE,{"derivedFrom":sQuery(id+"F3.wireOp",EDGE,"0df62e41-1287-4f69-95da-10b150b9bf08.trimOffspring")}),1.0]])]});
            var Q54;
            {var subQ0=sQuery(id+"F3.wireOp",EDGE,"36b8feae-4893-4e83-8179-12281b812430.trimOffspring");Q54=makeQuery(id+"F3.imprint","IMPRINT",FACE,{"disambiguationData":[TD([[makeQuery(id+"F3.imprint","IMPRINT",EDGE,{"derivedFrom":subQ0}),1.0]])]});}
            var Q55;
            Q55=makeQuery(id+"F3.imprint","IMPRINT",FACE,{"disambiguationData":[TD([[makeQuery(id+"F3.imprint","IMPRINT",EDGE,{"derivedFrom":sQuery(id+"F3.wireOp",EDGE,"fd2fb7f9-af83-47ea-9c70-553f0d0352ca.trimOffspring")}),1.0]])]});
            var Q56;
            Q56=makeQuery(id+"F3.imprint","IMPRINT",FACE,{"disambiguationData":[TD([[makeQuery(id+"F3.imprint","IMPRINT",EDGE,{"derivedFrom":sQuery(id+"F3.wireOp",EDGE,"b38b1c50-6a93-4044-a3e5-90237b3e0558.trimOffspring")}),-1.0]])]});
            var Q57;
            Q57=makeQuery(id+"F3.imprint","IMPRINT",FACE,{"disambiguationData":[TD([[makeQuery(id+"F3.imprint","IMPRINT",EDGE,{"derivedFrom":sQuery(id+"F3.wireOp",EDGE,"f0d25497-838d-4696-a3a2-9b4ae3221af0.trimOffspring")}),1.0]])]});
            var Q58;
            Q58=makeQuery(id+"F3.imprint","IMPRINT",FACE,{"disambiguationData":[TD([[makeQuery(id+"F3.imprint","IMPRINT",EDGE,{"derivedFrom":sQuery(id+"F3.wireOp",EDGE,"af33d477-2f43-4241-a502-9f7889e40a5c.trimOffspring")}),1.0]])]});
            var Q59;
            Q59=makeQuery(id+"F3.imprint","IMPRINT",FACE,{"disambiguationData":[TD([[makeQuery(id+"F3.imprint","IMPRINT",EDGE,{"derivedFrom":sQuery(id+"F3.wireOp",EDGE,"78126fb9-9eca-41aa-bf8f-ff432425a166.trimOffspring")}),-1.0]])]});
            var Q60;
            {var subQ0=sQuery(id+"F3.wireOp",EDGE,"Sf0W1LvG-PSwA-hiG2-Qytt-6ozFxqWG3eeh.bottom");Q60=makeQuery(id+"F3.imprint","IMPRINT",FACE,{"disambiguationData":[TD([[makeQuery(id+"F3.imprint","IMPRINT",EDGE,{"derivedFrom":subQ0}),1.0]])]});}
            var Q61;
            {var subQ0=sQuery(id+"F3.wireOp",EDGE,"Sf0W1LvG-PSwA-hiG2-Qytt-6ozFxqWG3eeh.top");Q61=makeQuery(id+"F3.imprint","IMPRINT",FACE,{"disambiguationData":[TD([[makeQuery(id+"F3.imprint","IMPRINT",EDGE,{"derivedFrom":subQ0}),-1.0]])]});}
            var Q62;
            Q62=makeQuery(id+"F3.imprint","IMPRINT",FACE,{"disambiguationData":[TD([[makeQuery(id+"F3.imprint","IMPRINT",EDGE,{"derivedFrom":sQuery(id+"F3.wireOp",EDGE,"c02d6e47-0b4d-44c2-9b90-46bcdeab543a.trimOffspring")}),-1.0]])]});
            var Q63;
            Q63=makeQuery(id+"F3.imprint","IMPRINT",FACE,{"disambiguationData":[TD([[makeQuery(id+"F3.imprint","IMPRINT",EDGE,{"derivedFrom":sQuery(id+"F3.wireOp",EDGE,"8ea9c854-bcba-4ece-8b5a-eace405d1142.trimOffspring")}),-1.0]])]});
            var Q64;
            Q64=makeQuery(id+"F3.imprint","IMPRINT",FACE,{"disambiguationData":[TD([[makeQuery(id+"F3.imprint","IMPRINT",EDGE,{"derivedFrom":sQuery(id+"F3.wireOp",EDGE,"18fb3a82-bf3e-4e4d-a53c-a3effed06204.trimOffspring")}),-1.0]])]});
            var Q65;
            Q65=makeQuery(id+"F3.imprint","IMPRINT",FACE,{"disambiguationData":[TD([[makeQuery(id+"F3.imprint","IMPRINT",EDGE,{"derivedFrom":sQuery(id+"F3.wireOp",EDGE,"dea5a405-b210-4b61-8359-fbd126c4a1c9.trimOffspring")}),-1.0]])]});
            var Q66;
            {var subQ0=sQuery(id+"F3.wireOp",EDGE,"2e86fdf9-5eb1-4d1c-8c3e-26e158b78705.trimOffspring");Q66=makeQuery(id+"F3.imprint","IMPRINT",FACE,{"disambiguationData":[TD([[makeQuery(id+"F3.imprint","IMPRINT",EDGE,{"derivedFrom":subQ0}),-1.0]])]});}
            var Q67;
            {var subQ0=sQuery(id+"F3.wireOp",EDGE,"E26.trimOffspring");Q67=makeQuery(id+"F3.imprint","IMPRINT",FACE,{"disambiguationData":[TD([[makeQuery(id+"F3.imprint","IMPRINT",EDGE,{"derivedFrom":subQ0}),-1.0]])]});}
            var Q68;
            {var subQ0=sQuery(id+"F3.wireOp",EDGE,"E25.top");Q68=makeQuery(id+"F3.imprint","IMPRINT",FACE,{"disambiguationData":[TD([[makeQuery(id+"F3.imprint","IMPRINT",EDGE,{"derivedFrom":subQ0}),-1.0]])]});}
            var Q69;
            Q69=makeQuery(id+"F3.imprint","IMPRINT",FACE,{"disambiguationData":[TD([[makeQuery(id+"F3.imprint","IMPRINT",EDGE,{"derivedFrom":sQuery(id+"F3.wireOp",EDGE,"E29.trimOffspring")}),1.0]])]});
            var Q70;
            Q70=makeQuery(id+"F3.imprint","IMPRINT",FACE,{"disambiguationData":[TD([[makeQuery(id+"F3.imprint","IMPRINT",EDGE,{"derivedFrom":sQuery(id+"F3.wireOp",EDGE,"E33.trimOffspring")}),1.0]])]});
            var Q71;
            Q71=makeQuery(id+"F3.imprint","IMPRINT",FACE,{"disambiguationData":[TD([[makeQuery(id+"F3.imprint","IMPRINT",EDGE,{"derivedFrom":sQuery(id+"F3.wireOp",EDGE,"E37.trimOffspring")}),-1.0]])]});
            var Q72;
            Q72=makeQuery(id+"F3.imprint","IMPRINT",FACE,{"disambiguationData":[TD([[makeQuery(id+"F3.imprint","IMPRINT",EDGE,{"derivedFrom":sQuery(id+"F3.wireOp",EDGE,"E45.trimOffspring")}),1.0]])]});
            var Q73;
            Q73=makeQuery(id+"F3.imprint","IMPRINT",FACE,{"disambiguationData":[TD([[makeQuery(id+"F3.imprint","IMPRINT",EDGE,{"derivedFrom":sQuery(id+"F3.wireOp",EDGE,"E49.trimOffspring")}),1.0]])]});
            var Q74;
            Q74=makeQuery(id+"F3.imprint","IMPRINT",FACE,{"disambiguationData":[TD([[makeQuery(id+"F3.imprint","IMPRINT",EDGE,{"derivedFrom":sQuery(id+"F3.wireOp",EDGE,"E53.trimOffspring")}),1.0]])]});
            var Q75;
            Q75=makeQuery(id+"F3.imprint","IMPRINT",FACE,{"disambiguationData":[TD([[makeQuery(id+"F3.imprint","IMPRINT",EDGE,{"derivedFrom":sQuery(id+"F3.wireOp",EDGE,"E57.trimOffspring")}),1.0]])]});
            var Q76;
            {var subQ2=sQuery(id+"F3.wireOp",EDGE,"E23.top");Q76=makeQuery(id+"F3.imprint","IMPRINT",FACE,{"disambiguationData":[TD([[makeQuery(id+"F3.imprint","IMPRINT",EDGE,{"derivedFrom":subQ2}),-1.0]])]});}
            var Q77;
            Q77=makeQuery(id+"F3.imprint","IMPRINT",FACE,{"disambiguationData":[TD([[makeQuery(id+"F3.imprint","IMPRINT",EDGE,{"derivedFrom":sQuery(id+"F3.wireOp",EDGE,"E62.trimOffspring")}),-1.0]])]});
            var Q78;
            Q78=makeQuery(id+"F3.imprint","IMPRINT",FACE,{"disambiguationData":[TD([[makeQuery(id+"F3.imprint","IMPRINT",EDGE,{"derivedFrom":sQuery(id+"F3.wireOp",EDGE,"E65.trimOffspring")}),1.0]])]});
            var Q79;
            Q79=makeQuery(id+"F3.imprint","IMPRINT",FACE,{"disambiguationData":[TD([[makeQuery(id+"F3.imprint","IMPRINT",EDGE,{"derivedFrom":sQuery(id+"F3.wireOp",EDGE,"E69.trimOffspring")}),1.0]])]});
            var Q80;
            Q80=makeQuery(id+"F3.imprint","IMPRINT",FACE,{"disambiguationData":[TD([[makeQuery(id+"F3.imprint","IMPRINT",EDGE,{"derivedFrom":sQuery(id+"F3.wireOp",EDGE,"E73.trimOffspring")}),1.0]])]});
            var Q81;
            Q81=makeQuery(id+"F3.imprint","IMPRINT",FACE,{"disambiguationData":[TD([[makeQuery(id+"F3.imprint","IMPRINT",EDGE,{"derivedFrom":sQuery(id+"F3.wireOp",EDGE,"E82.trimOffspring")}),-1.0]])]});
            var Q82;
            Q82=makeQuery(id+"F3.imprint","IMPRINT",FACE,{"disambiguationData":[TD([[makeQuery(id+"F3.imprint","IMPRINT",EDGE,{"derivedFrom":sQuery(id+"F3.wireOp",EDGE,"E85.trimOffspring")}),1.0]])]});
            var Q83;
            Q83=makeQuery(id+"F3.imprint","IMPRINT",FACE,{"disambiguationData":[TD([[makeQuery(id+"F3.imprint","IMPRINT",EDGE,{"derivedFrom":sQuery(id+"F3.wireOp",EDGE,"E89.trimOffspring")}),1.0]])]});
            var Q84;
            Q84=makeQuery(id+"F3.imprint","IMPRINT",FACE,{"disambiguationData":[TD([[makeQuery(id+"F3.imprint","IMPRINT",EDGE,{"derivedFrom":sQuery(id+"F3.wireOp",EDGE,"E93.trimOffspring")}),1.0]])]});
            var Q85;
            Q85=makeQuery(id+"F3.imprint","IMPRINT",FACE,{"disambiguationData":[TD([[makeQuery(id+"F3.imprint","IMPRINT",EDGE,{"derivedFrom":sQuery(id+"F3.wireOp",EDGE,"E97.trimOffspring")}),1.0]])]});
            var Q86;
            {var subQ0=sQuery(id+"F3.wireOp",EDGE,"E99.trimOffspring");Q86=makeQuery(id+"F3.imprint","IMPRINT",FACE,{"disambiguationData":[TD([[makeQuery(id+"F3.imprint","IMPRINT",EDGE,{"derivedFrom":subQ0}),-1.0]])]});}
            var Q87;
            {var subQ0=sQuery(id+"F3.wireOp",EDGE,"E20.right");Q87=makeQuery(id+"F3.imprint","IMPRINT",FACE,{"disambiguationData":[TD([[makeQuery(id+"F3.imprint","IMPRINT",EDGE,{"derivedFrom":subQ0}),1.0]])]});}
            var Q88;
            {var subQ0=sQuery(id+"F3.wireOp",EDGE,"E105.trimOffspring");Q88=makeQuery(id+"F3.imprint","IMPRINT",FACE,{"disambiguationData":[TD([[makeQuery(id+"F3.imprint","IMPRINT",EDGE,{"derivedFrom":subQ0}),1.0]])]});}
            var Q89;
            {var subQ0=sQuery(id+"F3.wireOp",EDGE,"E109.trimOffspring");Q89=makeQuery(id+"F3.imprint","IMPRINT",FACE,{"disambiguationData":[TD([[makeQuery(id+"F3.imprint","IMPRINT",EDGE,{"derivedFrom":subQ0}),1.0]])]});}
            var Q90;
            {var subQ0=sQuery(id+"F3.wireOp",EDGE,"E113.trimOffspring");Q90=makeQuery(id+"F3.imprint","IMPRINT",FACE,{"disambiguationData":[TD([[makeQuery(id+"F3.imprint","IMPRINT",EDGE,{"derivedFrom":subQ0}),1.0]])]});}
            var Q91;
            {var subQ4=sQuery(id+"F3.wireOp",EDGE,"E21.bottom");Q91=makeQuery(id+"F3.imprint","IMPRINT",FACE,{"disambiguationData":[TD([[makeQuery(id+"F3.imprint","IMPRINT",EDGE,{"derivedFrom":subQ4}),-1.0]])]});}
            extrude(context, id + "F4", {"entities" : qUnion([Q0, Q1, Q2, Q3, Q4, Q5, Q6, Q7, Q8, Q9, Q10, Q11, Q12, Q13, Q14, Q15, Q16, Q17, Q18, Q19, Q20, Q21, Q22, Q23, Q24, Q25, Q26, Q27, Q28, Q29, Q30, Q31, Q32, Q33, Q34, Q35, Q36, Q37, Q38, Q39, Q40, Q41, Q42, Q43, Q44, Q45, Q46, Q47, Q48, Q49, Q50, Q51, Q52, Q53, Q54, Q55, Q56, Q57, Q58, Q59, Q60, Q61, Q62, Q63, Q64, Q65, Q66, Q67, Q68, Q69, Q70, Q71, Q72, Q73, Q74, Q75, Q76, Q77, Q78, Q79, Q80, Q81, Q82, Q83, Q84, Q85, Q86, Q87, Q88, Q89, Q90, Q91]), "operationType" : NewBodyOperationType.REMOVE, "oppositeDirection" : true, "depth" : 50.8 * mm, "offsetDistance" : 25.4 * mm});
        }
    });
